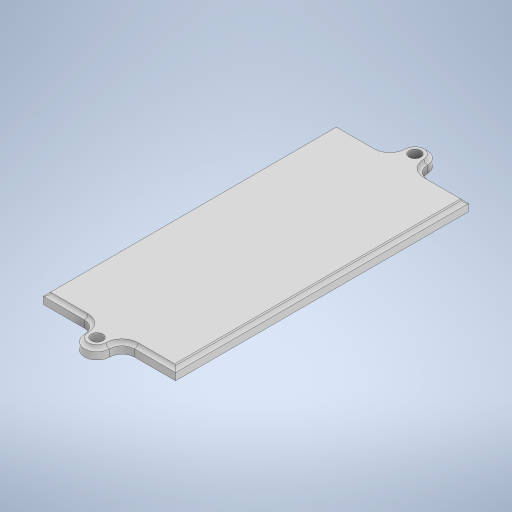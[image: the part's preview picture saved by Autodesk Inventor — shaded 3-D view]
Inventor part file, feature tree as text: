
AUTODESK INVENTOR PART (.ipt)
format: ipt  version: 2024.2 (Build 282272000, 272)  size: 471,552 bytes
history: native  units: in
note: dims shown in document units (in); Inventor stores cm internally (conversion verified against a paired STEP export)
features: sketch x3, extrude x2, chamfer x2, fillet x1
ambient origin geometry x8: Origin, YZ Plane, XZ Plane, XY Plane, X Axis, Y Axis, Z Axis, Center Point
bodies: Solid1 (feature_tree)
feature tree (8):
  extrude  "Extrusion1"  Depth=3.2283in
  fillet  "Fillet1"  Radius=3.2283in
  sketch  "Sketch2"  dims[d3=0.1299in]
  chamfer  "Chamfer1"  Distance=0.1299in
  extrude  "Extrusion3"  Depth=0.1378in
  chamfer  "Chamfer2"  Distance=0.7283in
  sketch  "Sketch1"  dims[d0=0.1378in d1=1.4567in d2=3.2283in]
  sketch  "Sketch3"  dims[d4=0.7283in d5=0.1299in d6=0.1378in d7=0.7283in d8=0.2756in d9=0.1378in d10=0.1181in d11=0.0in d12=0.0394in d13=0.0787in d14=0.0787in d15=0.0787in d16=0.0787in d17=0.0787in d18=135.0deg d20=0.0787in d21=0.0787in d22=0.0787in d23=0.0787in d24=0.0787in d25=0.0787in d26=0.0787in d28=135.0deg d29=0.0787in d30=0.0787in d31=0.0787in d32=0.0787in d33=45.0deg d35=0.0787in d36=0.0787in d39=0.0787in d40=0.0787in d41=0.0787in d42=0.0787in d43=0.0787in d44=0.0394in d45=0.1575in d50=0.1181in d51=0.0787in d52=0.0787in d53=0.0787in d54=0.0787in d55=0.0in d58=0.0098in d59=0.0787in d60=45.0deg d61=0.1378in d62=0.1378in d63=0.1378in d64=0.1378in d65=0.1378in d66=135.0deg d67=0.1378in d68=0.1378in d69=0.1378in d70=0.1378in d71=0.1378in d72=0.1378in d73=0.1378in d74=135.0deg d75=0.1378in d76=0.1378in d77=0.1378in d78=0.1378in d79=45.0deg d80=0.1378in d81=0.1378in d82=0.1378in d83=0.1378in d84=0.1378in d85=0.1378in d86=0.1378in d87=0.0689in d88=0.2756in d89=0.2067in d90=0.1378in d91=0.1378in d92=0.1378in d93=0.1378in d94=0.0in d96=0.0787in d97=0.0in d98=0.0591in d99=0.0787in d100=45.0deg]
